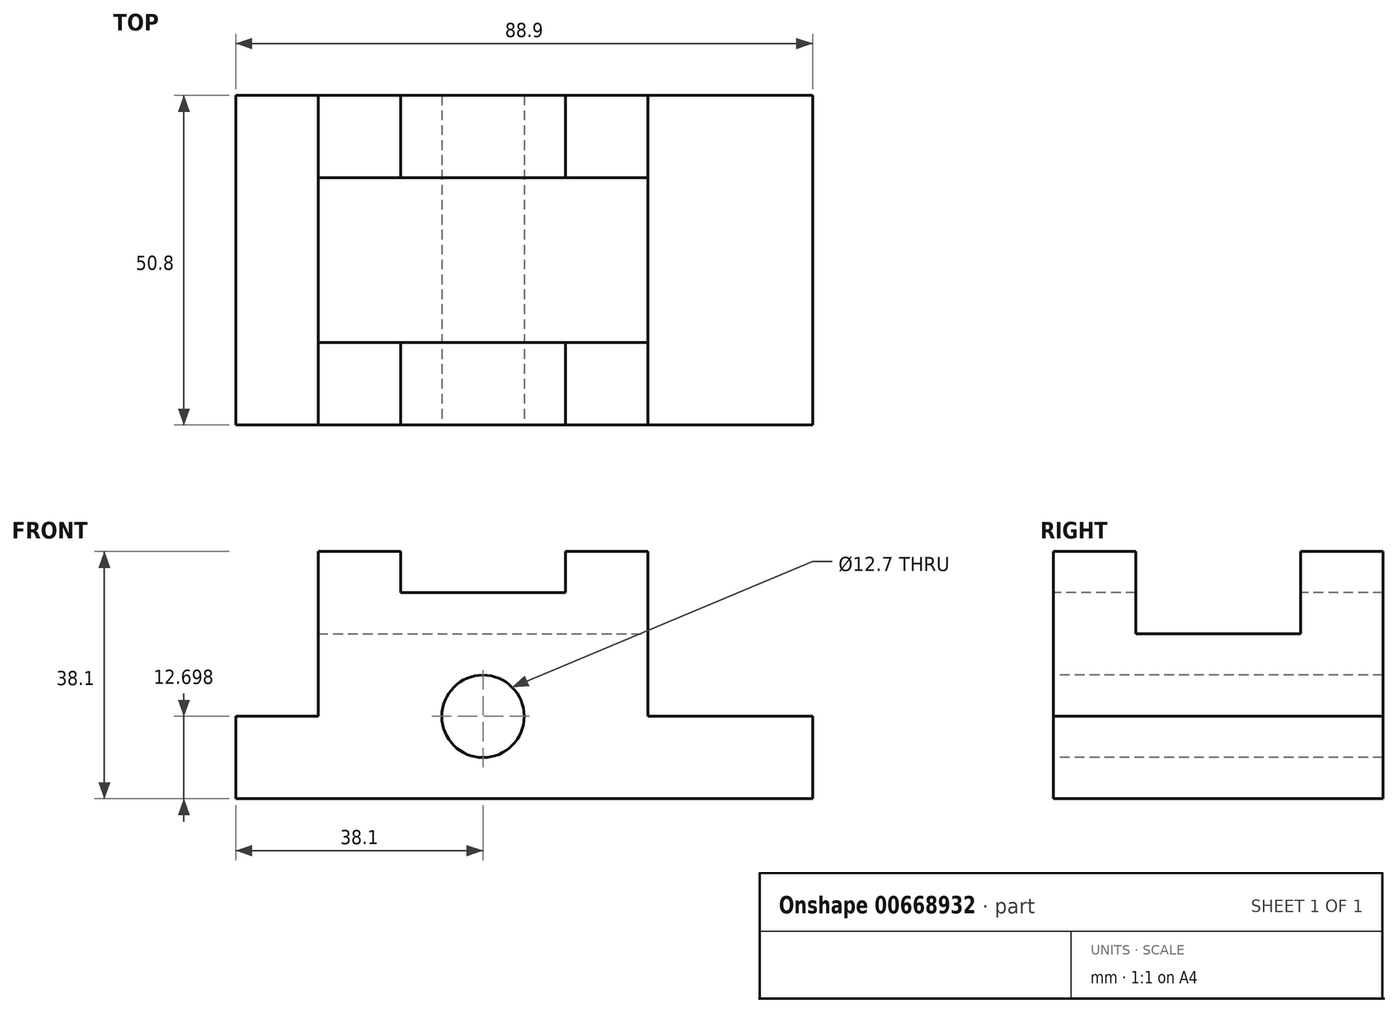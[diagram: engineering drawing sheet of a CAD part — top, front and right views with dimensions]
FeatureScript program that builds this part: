
annotation { "Feature Type Name" : "Feature", "Feature Type Description" : "" }
export const myFeature = defineFeature(function(context is Context, id is Id, definition is map)
    precondition{}
    {
        {
            var Q0;
            Q0=qCreatedBy(makeId("Front.planeOp"),FACE);
            var sketch = newSketch(context, id + "F0", { "sketchPlane" : qUnion([Q0])});
            skLineSegment(sketch, "E0.bottom", {"start": v(-44.6, 10.57) * mm, "end": v(44.3, 10.57) * mm});
            skLineSegment(sketch, "E0.top", {"start": v(-44.6, -27.53) * mm, "end": v(44.3, -27.53) * mm});
            skLineSegment(sketch, "E0.left", {"start": v(-44.6, 10.57) * mm, "end": v(-44.6, -27.53) * mm});
            skLineSegment(sketch, "E0.right", {"start": v(44.3, 10.57) * mm, "end": v(44.3, -27.53) * mm});
            skSolve(sketch);
        }
        {
            var Q0;
            Q0 = qSketchRegion(id + "F0", true);
            extrude(context, id + "F1", {"entities" : qUnion([Q0]), "depth" : 50.8 * mm, "offsetDistance" : 25.4 * mm});
        }
        {
            var Q0;
            Q0=makeQuery(id+"F1.opExtrude","CAP_FACE",FACE,{"disambiguationData":[OSD([sQuery(id+"F0.wireOp",EDGE,"E0.bottom"),sQuery(id+"F0.wireOp",EDGE,"E0.top"),sQuery(id+"F0.wireOp",EDGE,"E0.left"),sQuery(id+"F0.wireOp",EDGE,"E0.right")])],"isStart":false});
            var sketch = newSketch(context, id + "F2", { "sketchPlane" : qUnion([Q0])});
            skLineSegment(sketch, "E1.bottom", {"start": v(-44.6, 10.57) * mm, "end": v(-31.9, 10.57) * mm});
            skLineSegment(sketch, "E1.top", {"start": v(-44.6, -14.83) * mm, "end": v(-31.9, -14.83) * mm});
            skLineSegment(sketch, "E1.left", {"start": v(-44.6, 10.57) * mm, "end": v(-44.6, -14.83) * mm});
            skLineSegment(sketch, "E1.right", {"start": v(-31.9, 10.57) * mm, "end": v(-31.9, -14.83) * mm});
            skSolve(sketch);
        }
        {
            var Q0;
            Q0 = qSketchRegion(id + "F2", true);
            extrude(context, id + "F3", {"entities" : qUnion([Q0]), "operationType" : NewBodyOperationType.REMOVE, "oppositeDirection" : true, "depth" : 50.8 * mm, "offsetDistance" : 25.4 * mm});
        }
        {
            var Q0;
            Q0=makeQuery(id+"F1.opExtrude","CAP_FACE",FACE,{"disambiguationData":[OSD([sQuery(id+"F0.wireOp",EDGE,"E0.bottom"),sQuery(id+"F0.wireOp",EDGE,"E0.top"),sQuery(id+"F0.wireOp",EDGE,"E0.left"),sQuery(id+"F0.wireOp",EDGE,"E0.right")])],"isStart":false});
            var sketch = newSketch(context, id + "F4", { "sketchPlane" : qUnion([Q0])});
            skLineSegment(sketch, "E2.bottom", {"start": v(-19.2, 10.57) * mm, "end": v(6.2, 10.57) * mm});
            skLineSegment(sketch, "E2.top", {"start": v(-19.2, 4.22) * mm, "end": v(6.2, 4.22) * mm});
            skLineSegment(sketch, "E2.left", {"start": v(-19.2, 10.57) * mm, "end": v(-19.2, 4.22) * mm});
            skLineSegment(sketch, "E2.right", {"start": v(6.2, 10.57) * mm, "end": v(6.2, 4.22) * mm});
            skSolve(sketch);
        }
        {
            var Q0;
            Q0 = qSketchRegion(id + "F4", true);
            extrude(context, id + "F5", {"entities" : qUnion([Q0]), "operationType" : NewBodyOperationType.REMOVE, "oppositeDirection" : true, "depth" : 50.8 * mm, "offsetDistance" : 25.4 * mm});
        }
        {
            var Q0;
            Q0=makeQuery(id+"F1.opExtrude","CAP_FACE",FACE,{"disambiguationData":[OSD([sQuery(id+"F0.wireOp",EDGE,"E0.bottom"),sQuery(id+"F0.wireOp",EDGE,"E0.top"),sQuery(id+"F0.wireOp",EDGE,"E0.left"),sQuery(id+"F0.wireOp",EDGE,"E0.right")])],"isStart":false});
            var sketch = newSketch(context, id + "F6", { "sketchPlane" : qUnion([Q0])});
            skLineSegment(sketch, "E3.bottom", {"start": v(44.3, 10.57) * mm, "end": v(18.9, 10.57) * mm});
            skLineSegment(sketch, "E3.top", {"start": v(44.3, -14.83) * mm, "end": v(18.9, -14.83) * mm});
            skLineSegment(sketch, "E3.left", {"start": v(44.3, 10.57) * mm, "end": v(44.3, -14.83) * mm});
            skLineSegment(sketch, "E3.right", {"start": v(18.9, 10.57) * mm, "end": v(18.9, -14.83) * mm});
            skSolve(sketch);
        }
        {
            var Q0;
            Q0 = qSketchRegion(id + "F6", true);
            extrude(context, id + "F7", {"entities" : qUnion([Q0]), "operationType" : NewBodyOperationType.REMOVE, "oppositeDirection" : true, "depth" : 50.8 * mm, "offsetDistance" : 25.4 * mm});
        }
        {
            var Q0;
            Q0=makeQuery(id+"F7.boolean.opBoolean","COPY",FACE,{"derivedFrom":makeQuery(id+"F7.opExtrude","SWEPT_FACE",FACE,{"disambiguationData":[OSD([sQuery(id+"F6.wireOp",EDGE,"E3.right")])]})});
            var sketch = newSketch(context, id + "F8", { "sketchPlane" : qUnion([Q0])});
            skLineSegment(sketch, "E4.bottom", {"start": v(-38.1, 10.57) * mm, "end": v(-12.7, 10.57) * mm});
            skLineSegment(sketch, "E4.top", {"start": v(-38.1, -2.13) * mm, "end": v(-12.7, -2.13) * mm});
            skLineSegment(sketch, "E4.left", {"start": v(-38.1, 10.57) * mm, "end": v(-38.1, -2.13) * mm});
            skLineSegment(sketch, "E4.right", {"start": v(-12.7, 10.57) * mm, "end": v(-12.7, -2.13) * mm});
            skSolve(sketch);
        }
        {
            var Q0;
            Q0 = qSketchRegion(id + "F8", true);
            extrude(context, id + "F9", {"entities" : qUnion([Q0]), "operationType" : NewBodyOperationType.REMOVE, "oppositeDirection" : true, "depth" : 88.9 * mm, "offsetDistance" : 25.4 * mm});
        }
        {
            var Q0;
            Q0=makeQuery(id+"F1.opExtrude","CAP_FACE",FACE,{"disambiguationData":[OSD([sQuery(id+"F0.wireOp",EDGE,"E0.bottom"),sQuery(id+"F0.wireOp",EDGE,"E0.top"),sQuery(id+"F0.wireOp",EDGE,"E0.left"),sQuery(id+"F0.wireOp",EDGE,"E0.right")])],"isStart":false});
            var sketch = newSketch(context, id + "F10", { "sketchPlane" : qUnion([Q0])});
            skCircle(sketch, "E5", {"center": v(-6.5, -14.83) * mm, "radius": 6.35 * mm});
            skSolve(sketch);
        }
        {
            var Q0;
            Q0 = qSketchRegion(id + "F10", true);
            extrude(context, id + "F11", {"entities" : qUnion([Q0]), "operationType" : NewBodyOperationType.REMOVE, "oppositeDirection" : true, "depth" : 50.8 * mm, "offsetDistance" : 25.4 * mm});
        }
    });
